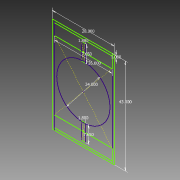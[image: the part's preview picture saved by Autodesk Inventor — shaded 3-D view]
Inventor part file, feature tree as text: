
AUTODESK INVENTOR PART (.ipt)
format: ipt  version: 2014 SP1 (Build 180222100, 222)  size: 81,920 bytes
history: native  units: in
note: dims shown in document units (in); Inventor stores cm internally (conversion verified against a paired STEP export)
features: sketch x1
ambient origin geometry x8: Origin, YZ Plane, XZ Plane, XY Plane, X Axis, Y Axis, Z Axis, Center Point
feature tree (1):
  sketch  "Sketch1"  dims[d2=1.8in d3=7.65in d4=1.8in d5=7.65in d7=24.0in d13=1.0in d14=26.0in d15=43.0in d16=28.0in]
